# Revit family: Hager-VOLTA-Surface_mounted-IP30-With_Cover-With_DIN-Hosted-CH-it
name_source: partatom
category: Electrical Equipment
units: mm (PartAtom-declared; Revit-internal decimal feet)

## family parameters
Cut with Voids When Loaded = No
Host = Face
Maintain Annotation Orientation = Yes
Panel Configuration = Two Columns, Circuits Across
Part Type = Panelboard
Room Calculation Point = No
Round Connector Dimension = Use Diameter
Shared = No

## types (10) — shared parameters
BC_MODEL_ID = 1547133
BC_OBJECT_ID = 513471
BC_OBJECT_VERSION = #9
Code hager = ADD-EC000214_EU
EF000003 - modo di montaggio = apparente
EF000008 - larghezza = 305 mm  [stored 1.00066 ft]
EF000024 - resistente ai raggi UV = No
EF000049 - profondità = 96 mm  [stored 0.314961 ft]
EF000116 - numero RAL = 9010
EF001062 - versione EMC = No
EF001134 - barra DIN = Yes
EF002950 - numero di unità modulari = 12
EF005474 - grado di protezione (IP) = IP30
EF006244 - coperchio/porta trasparente = No
EF006306 - con serratura = No
EF015777 - morsettiera a conduttore neutro = No
ETIM class code = EC000214
ETIM class name = Small distribution board
HG000001 - Numero di colonne = 1
HG000002-with door or cover-it = Yes
HG000003-Range-it = VOLTA
HG000005-Thickness-it = 2 mm  [stored 0.00656168 ft]
HG000006-Flush mounted-it = No
HG000009-Double swing door-it = No
HG000010-Asymmetric doors-it = No
HG000012-Door swing angle-it = 90.00°
HG000013-Door on the left-it = No
HG000014-Door on the right-it = Yes
HG000015-Clearance visibility-it = Yes
HG000016-Door 3D visibility-it = Yes
HG000017-Distance between poles-it = 18 mm  [stored 0.0590551 ft]
HG000060-RAL-number = 9010
HG000099-Onfly Template ID-it-CH = 507532
HGEF0002950-larghezza in unità di suddivisione = 12
Manufacturer = Hager
Name = VOLTA-Surface_mounted-IP30-With_Cover-With_DIN-CH
Name BIM&CO = Electricity
Name hager = ADD_Enclosures_EC000214
Uniformat = Low Tension Service & Dist.
Uniformat code = D501001
zero-valued in all types: Default Elevation, EF000218 - profondità di montaggio, EF000846 - larghezza di montaggio, EF001131 - profondità interna, HG000007-Number of empty columns-it

## per-type parameters (varying)
| type | BC_VARIANT_ID | EF000007 - colore | EF000040 - altezza | EF000118 - con piastra di montaggio | EF000266 - numero di file | EF000332 - altezza di installazione | EF001088 - possibilità di applicazione | EF004462 - tipo di chiusura | EF009212 - tipo di coperchio | EF015776 - morsetto di messa a terra | EF015941 - porta di trasmissione del segnale | HG000004-Manufacturer reference-it | HG000008-Number of empty rows-it | HG000011-Empty rows from bottom-it | HGEF000266-Numero di file |
| VOLTA-Surface_mounted_W305_H245_D96_12_Modular_Spacing-VA12A | 1174202 |  | 245 mm  [stored 0.803806 ft] | No | 1 | 0 mm  [stored 0 ft] | No |  |  | No | No | VA12A | 0 | No | 1 |
| VOLTA-Surface_mounted_W305_H370_D96_12_Modular_Spacing-VA24A | 1174203 | bianco | 370 mm  [stored 1.21391 ft] | No | 2 | 0 mm  [stored 0 ft] | Yes | altri | con taglio | Yes | No | VA24A | 0 | No | 2 |
| VOLTA-Surface_mounted_W305_H515_D96_12_Modular_Spacing-VA36A | 1174204 | bianco | 515 mm  [stored 1.68963 ft] | No | 3 | 0 mm  [stored 0 ft] | Yes | altri | con taglio | Yes | No | VA36A | 0 | No | 3 |
| VOLTA-Surface_mounted_W305_H515_D96_12_Modular_Spacing-VA36RM | 1174207 | bianco | 515 mm  [stored 1.68963 ft] | No | 3 | 0 mm  [stored 0 ft] | Yes | altri | con taglio | No | No | VA36RM | 0 | No | 3 |
| VOLTA-Surface_mounted_W305_H640_D96_12_Modular_Spacing-VA48A | 1174211 | bianco | 640 mm  [stored 2.09974 ft] | No | 4 | 0 mm  [stored 0 ft] | Yes | altri | con taglio | Yes | No | VA48A | 0 | No | 4 |
| VOLTA-Surface_mounted_W305_H765_D96_12_Modular_Spacing-VA602NWS | 1174212 | bianco | 765 mm  [stored 2.50984 ft] | Yes | 5 | 765 mm  [stored 2.50984 ft] | Yes | altri | con taglio | Yes | No | VA602NWS | 3 | Yes | 5 |
| VOLTA-Surface_mounted_W305_H765_D96_12_Modular_Spacing-VA602WWS | 1174213 | bianco | 765 mm  [stored 2.50984 ft] | Yes | 5 | 765 mm  [stored 2.50984 ft] | Yes | altri | con taglio | Yes | Yes | VA602WWS | 3 | Yes | 5 |
| VOLTA-Surface_mounted_W305_H765_D96_12_Modular_Spacing-VA603NWS | 1174214 | bianco | 765 mm  [stored 2.50984 ft] | Yes | 5 | 765 mm  [stored 2.50984 ft] | Yes | altri | con taglio | Yes | No | VA603NWS | 2 | Yes | 5 |
| VOLTA-Surface_mounted_W305_H765_D96_12_Modular_Spacing-VA603WWS | 1174215 | bianco | 765 mm  [stored 2.50984 ft] | Yes | 5 | 765 mm  [stored 2.50984 ft] | Yes | altri | con taglio | Yes | Yes | VA603WWS | 2 | Yes | 5 |
| VOLTA-Surface_mounted_W305_H765_D96_12_Modular_Spacing-VA60A | 1174216 | bianco | 765 mm  [stored 2.50984 ft] | No | 5 | 0 mm  [stored 0 ft] | Yes | altri | con taglio | Yes | No | VA60A | 0 | No | 5 |

note: column(s) folded — value = type name in every type: Reference

note: [stored X ft] marks values corroborated as IEEE doubles in the binary element streams (Revit-internal decimal feet)

## geometry (parser evidence)
native form markers: Sweep x15
no freeform markers — native parametric forms only
